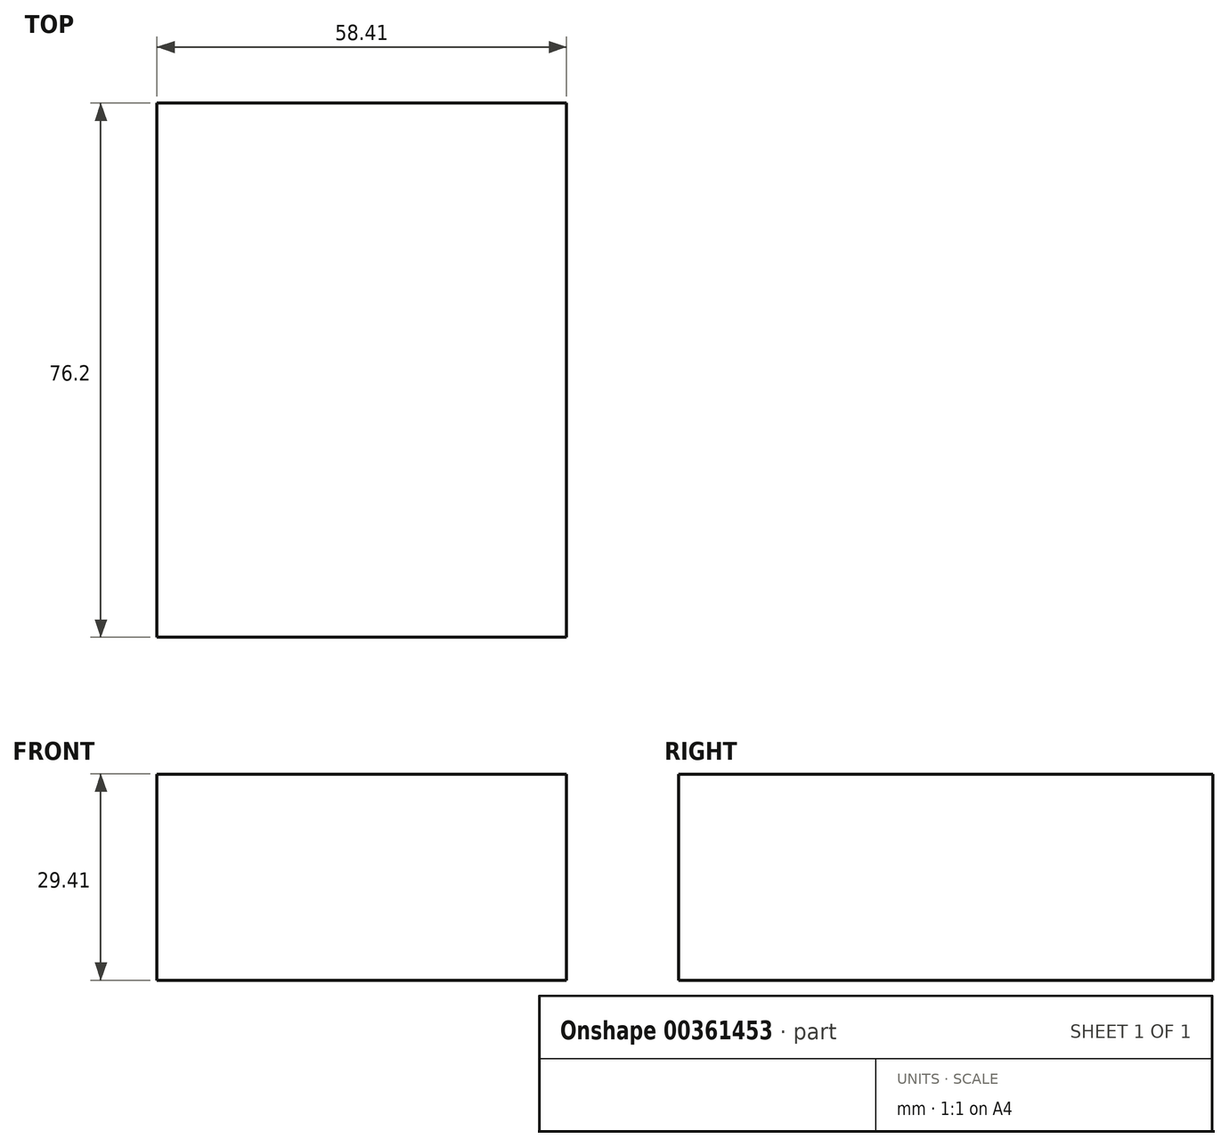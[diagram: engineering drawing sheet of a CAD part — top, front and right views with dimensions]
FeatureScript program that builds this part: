
annotation { "Feature Type Name" : "Feature", "Feature Type Description" : "" }
export const myFeature = defineFeature(function(context is Context, id is Id, definition is map)
    precondition{}
    {
        {
            var Q0;
            Q0=qCreatedBy(makeId("Front.planeOp"),FACE);
            var sketch = newSketch(context, id + "F0", { "sketchPlane" : qUnion([Q0])});
            skLineSegment(sketch, "E0.bottom", {"start": v(-58.41, 29.4) * mm, "end": v(0, 29.4) * mm});
            skLineSegment(sketch, "E0.top", {"start": v(-58.41, 0) * mm, "end": v(0, 0) * mm});
            skLineSegment(sketch, "E0.left", {"start": v(-58.41, 29.4) * mm, "end": v(-58.41, 0) * mm});
            skLineSegment(sketch, "E0.right", {"start": v(0, 29.4) * mm, "end": v(0, 0) * mm});
            skSolve(sketch);
        }
        {
            var Q0;
            Q0=makeQuery(id+"F0.imprint","IMPRINT",FACE,{"disambiguationData":[TD([[makeQuery(id+"F0.imprint","IMPRINT",EDGE,{"derivedFrom":sQuery(id+"F0.wireOp",EDGE,"E0.bottom")}),-1.0]])]});
            extrude(context, id + "F1", {"entities" : qUnion([Q0]), "depth" : 76.2 * mm});
        }
    });
